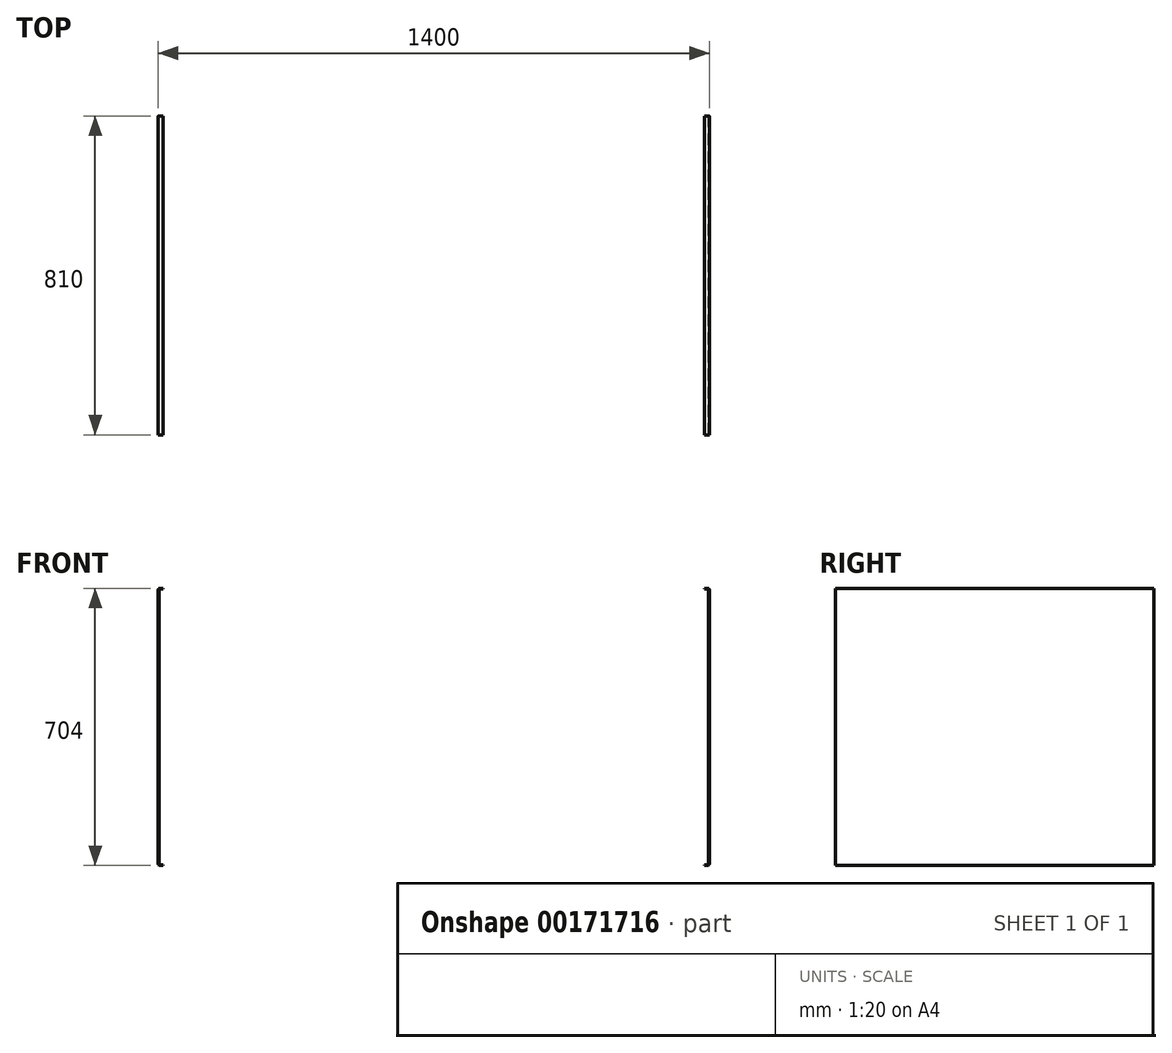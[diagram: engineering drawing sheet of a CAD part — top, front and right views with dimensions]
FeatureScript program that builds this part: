
annotation { "Feature Type Name" : "Feature", "Feature Type Description" : "" }
export const myFeature = defineFeature(function(context is Context, id is Id, definition is map)
    precondition{}
    {
        {
            var Q0;
            Q0=qCreatedBy(makeId("Front.planeOp"),FACE);
            var sketch = newSketch(context, id + "F0", { "sketchPlane" : qUnion([Q0])});
            skLineSegment(sketch, "E0", {"start": v(688, 318.4) * mm, "end": v(696, 318.4) * mm});
            skLineSegment(sketch, "E1", {"start": v(700, 314.4) * mm, "end": v(700, -381.6) * mm});
            skLineSegment(sketch, "E2", {"start": v(696, -385.6) * mm, "end": v(688, -385.6) * mm});
            skLineSegment(sketch, "E3", {"start": v(688, -385.6) * mm, "end": v(688, -383.6) * mm});
            skLineSegment(sketch, "E4", {"start": v(688, -383.6) * mm, "end": v(698, -383.6) * mm});
            skLineSegment(sketch, "E5", {"start": v(698, -383.6) * mm, "end": v(698, 316.4) * mm});
            skLineSegment(sketch, "E6", {"start": v(698, 316.4) * mm, "end": v(688, 316.4) * mm});
            skLineSegment(sketch, "E7", {"start": v(688, 316.4) * mm, "end": v(688, 318.4) * mm});
            skPoint(sketch, "E8.visualSharp", {"position": v(700, -385.6) * mm});
            skArc(sketch, "E8.filletArc", {"start": v(696, -385.6) * mm, "mid": v(698.83, -384.43) * mm, "end": v(700, -381.6) * mm});
            skPoint(sketch, "E9.visualSharp", {"position": v(700, 318.4) * mm});
            skArc(sketch, "E9.filletArc", {"start": v(700, 314.4) * mm, "mid": v(698.83, 317.23) * mm, "end": v(696, 318.4) * mm});
            skSolve(sketch);
        }
        {
            var Q0;
            Q0=makeQuery(id+"F0.imprint","IMPRINT",FACE,{"disambiguationData":[TD([[makeQuery(id+"F0.imprint","IMPRINT",EDGE,{"derivedFrom":sQuery(id+"F0.wireOp",EDGE,"E0")}),-1.0]])]});
            extrude(context, id + "F1", {"entities" : qUnion([Q0]), "endBound" : BoundingType.SYMMETRIC, "depth" : 810 * mm});
        }
        {
            var Q0;
            Q0=makeQuery(id+"F1.opExtrude","SWEPT_BODY",BODY,{"disambiguationData":[OSD([sQuery(id+"F0.wireOp",EDGE,"E0"),sQuery(id+"F0.wireOp",EDGE,"E1"),sQuery(id+"F0.wireOp",EDGE,"E2"),sQuery(id+"F0.wireOp",EDGE,"E3"),sQuery(id+"F0.wireOp",EDGE,"E4"),sQuery(id+"F0.wireOp",EDGE,"E5"),sQuery(id+"F0.wireOp",EDGE,"E6"),sQuery(id+"F0.wireOp",EDGE,"E7"),sQuery(id+"F0.wireOp",EDGE,"E8.filletArc"),sQuery(id+"F0.wireOp",EDGE,"E9.filletArc")])]});
            var Q1;
            Q1=qCreatedBy(makeId("Right.planeOp"),FACE);
            mirror(context, id + "F2", {"entities" : qUnion([Q0]), "mirrorPlane" : qUnion([Q1])});
        }
    });
